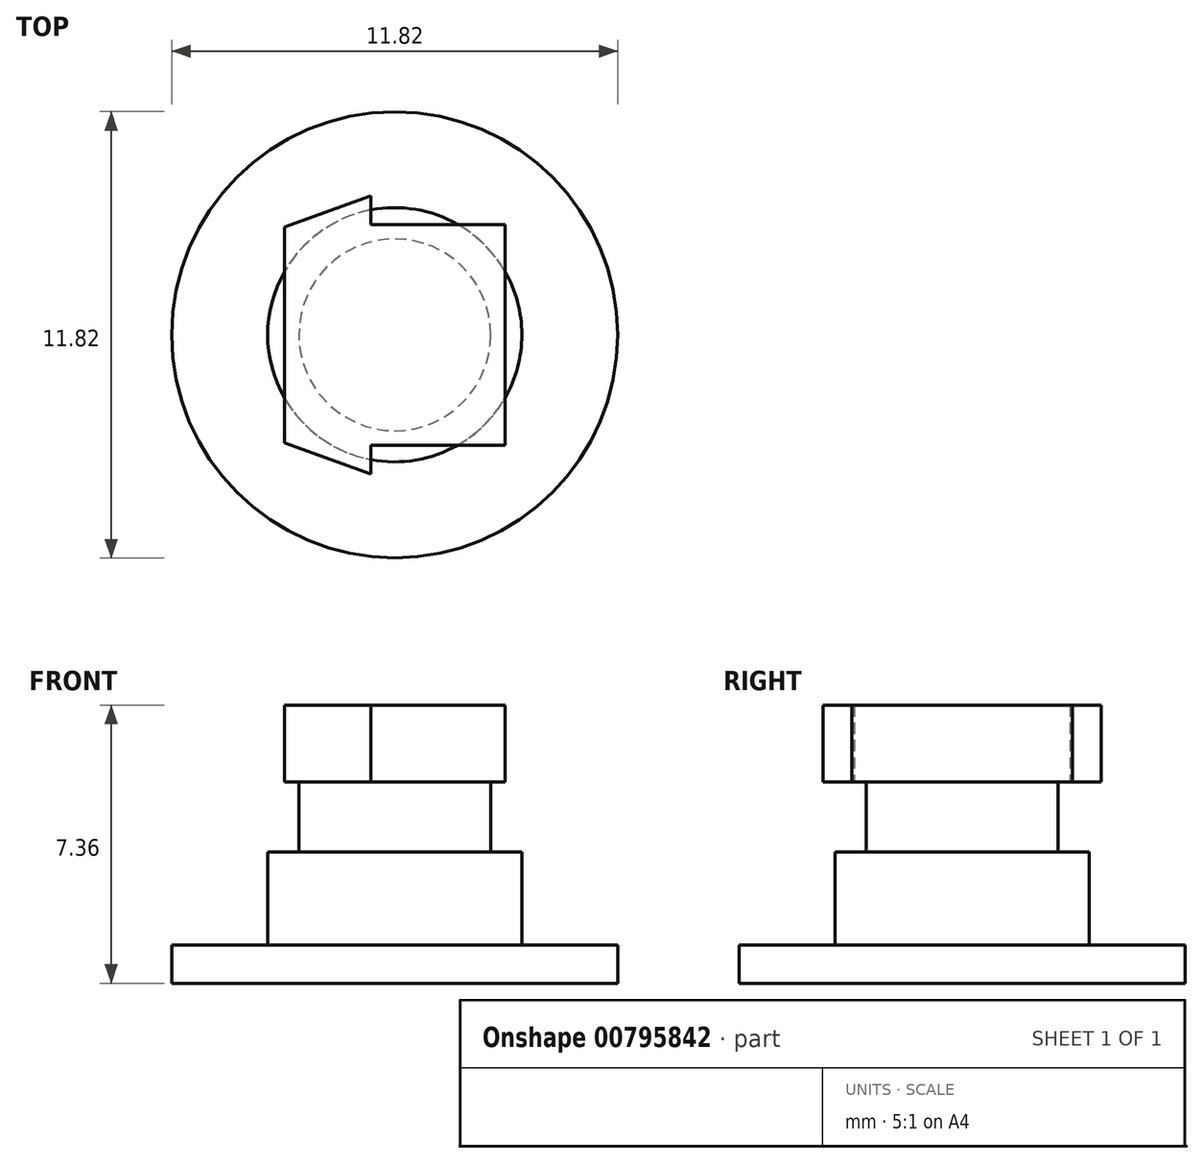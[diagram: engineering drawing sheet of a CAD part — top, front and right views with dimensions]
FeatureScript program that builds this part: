
annotation { "Feature Type Name" : "Feature", "Feature Type Description" : "" }
export const myFeature = defineFeature(function(context is Context, id is Id, definition is map)
    precondition{}
    {
        {
            var Q0;
            Q0=qCreatedBy(makeId("Front.planeOp"),FACE);
            var sketch = newSketch(context, id + "F0", { "sketchPlane" : qUnion([Q0])});
            skLineSegment(sketch, "E0", {"start": v(0, 0) * mm, "end": v(0, -5.33) * mm});
            skLineSegment(sketch, "E1", {"start": v(0, 0) * mm, "end": v(2.54, 0) * mm});
            skLineSegment(sketch, "E2", {"start": v(2.54, 0) * mm, "end": v(2.54, -1.85) * mm});
            skLineSegment(sketch, "E3", {"start": v(2.54, -1.85) * mm, "end": v(3.37, -1.85) * mm});
            skLineSegment(sketch, "E4", {"start": v(3.37, -1.85) * mm, "end": v(3.37, -4.32) * mm});
            skLineSegment(sketch, "E5", {"start": v(3.37, -4.32) * mm, "end": v(5.9, -4.32) * mm});
            skLineSegment(sketch, "E6", {"start": v(5.9, -4.32) * mm, "end": v(5.9, -5.33) * mm});
            skLineSegment(sketch, "E7", {"start": v(5.9, -5.33) * mm, "end": v(0, -5.33) * mm});
            skLineSegment(sketch, "E8", {"start": v(-33.51, 2.03) * mm, "end": v(30.63, 2.03) * mm, "construction": true});
            skSolve(sketch);
        }
        {
            var Q0;
            Q0=qCreatedBy(makeId("Front.planeOp"),FACE);
            var sketch = newSketch(context, id + "F1", { "sketchPlane" : qUnion([Q0])});
            skLineSegment(sketch, "E9", {"start": v(0, 28.95) * mm, "end": v(0, -18.87) * mm});
            skSolve(sketch);
        }
        {
            var Q0;
            Q0=makeQuery(id+"F0.imprint","IMPRINT",FACE,{"disambiguationData":[TD([[makeQuery(id+"F0.imprint","IMPRINT",EDGE,{"derivedFrom":sQuery(id+"F0.wireOp",EDGE,"E0")}),1.0]])]});
            var Q1;
            Q1=sQuery(id+"F1.wireOp",EDGE,"E9");
            revolve(context, id + "F2", {"surfaceOperationType" : NewSurfaceOperationType.NEW, "entities" : qUnion([Q0]), "axis" : qUnion([Q1]), "revolveType" : RevolveType.FULL});
        }
        {
            var Q0;
            Q0=qCreatedBy(makeId("Top.planeOp"),FACE);
            var sketch = newSketch(context, id + "F3", { "sketchPlane" : qUnion([Q0])});
            skLineSegment(sketch, "E10", {"start": v(-0.63, 2.92) * mm, "end": v(2.92, 2.92) * mm});
            skLineSegment(sketch, "E11", {"start": v(2.92, 2.92) * mm, "end": v(2.92, -2.92) * mm});
            skLineSegment(sketch, "E12", {"start": v(2.92, -2.92) * mm, "end": v(-0.63, -2.92) * mm});
            skLineSegment(sketch, "E13", {"start": v(-0.63, -2.92) * mm, "end": v(-0.63, -3.68) * mm});
            skLineSegment(sketch, "E14", {"start": v(-0.64, -3.68) * mm, "end": v(-2.92, -2.86) * mm});
            skLineSegment(sketch, "E15", {"start": v(-2.92, -2.86) * mm, "end": v(-2.92, 2.86) * mm});
            skLineSegment(sketch, "E16", {"start": v(-2.92, 2.86) * mm, "end": v(-0.64, 3.68) * mm});
            skLineSegment(sketch, "E17", {"start": v(-0.64, 3.68) * mm, "end": v(-0.64, 2.92) * mm});
            skSolve(sketch);
        }
        {
            var Q0;
            Q0=makeQuery(id+"F3.imprint","IMPRINT",FACE,{"disambiguationData":[TD([[makeQuery(id+"F3.imprint","IMPRINT",EDGE,{"derivedFrom":sQuery(id+"F3.wireOp",EDGE,"E10")}),-1.0]])]});
            extrude(context, id + "F4", {"entities" : qUnion([Q0]), "operationType" : NewBodyOperationType.ADD, "depth" : 2.03 * mm, "offsetDistance" : 25.4 * mm});
        }
    });
